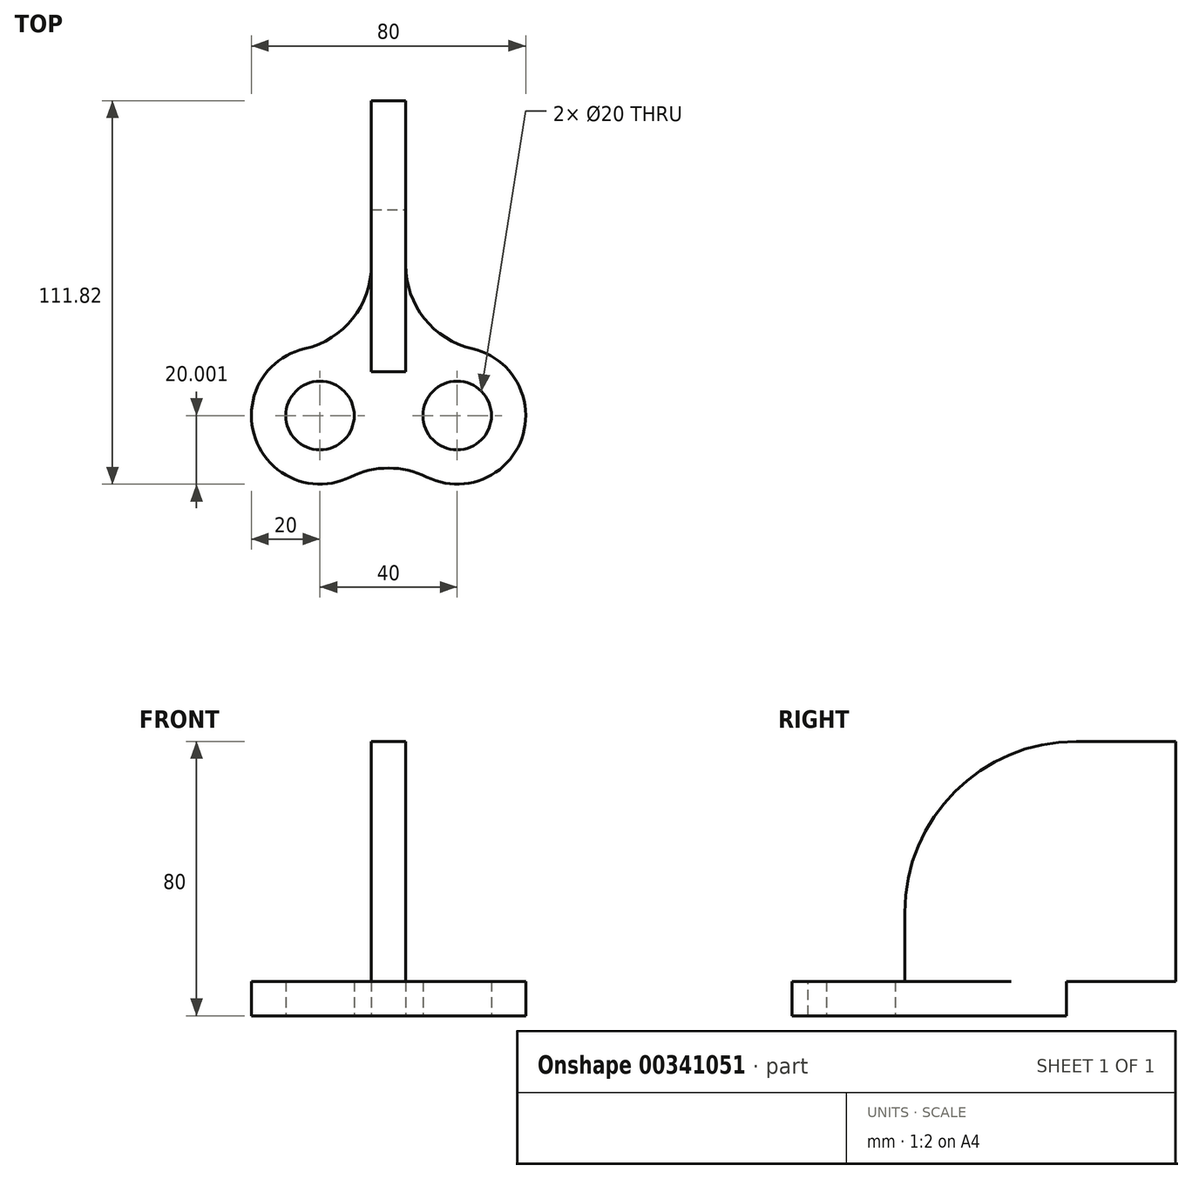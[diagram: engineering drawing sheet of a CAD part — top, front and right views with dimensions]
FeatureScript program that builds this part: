
annotation { "Feature Type Name" : "Feature", "Feature Type Description" : "" }
export const myFeature = defineFeature(function(context is Context, id is Id, definition is map)
    precondition{}
    {
        {
            var Q0;
            Q0=qCreatedBy(makeId("Top.planeOp"),FACE);
            var sketch = newSketch(context, id + "F0", { "sketchPlane" : qUnion([Q0])});
            skCircle(sketch, "E0", {"center": v(-20, 10.75) * mm, "radius": 20 * mm});
            skCircle(sketch, "E1", {"center": v(20, 10.75) * mm, "radius": 20 * mm});
            skCircle(sketch, "E2", {"center": v(-20, 10.75) * mm, "radius": 10 * mm});
            skCircle(sketch, "E3", {"center": v(20, 10.75) * mm, "radius": 10 * mm});
            skLineSegment(sketch, "E4.bottom", {"start": v(-5, 70.75) * mm, "end": v(5, 70.75) * mm});
            skLineSegment(sketch, "E4.top", {"start": v(-5, 10.75) * mm, "end": v(5, 10.75) * mm});
            skLineSegment(sketch, "E4.left", {"start": v(-5, 70.75) * mm, "end": v(-5, 10.75) * mm});
            skLineSegment(sketch, "E4.right", {"start": v(5, 70.75) * mm, "end": v(5, 10.75) * mm});
            skSolve(sketch);
        }
        {
            var Q0;
            Q0 = qSketchRegion(id + "F0", true);
            extrude(context, id + "F1", {"entities" : qUnion([Q0]), "depth" : 10 * mm});
        }
        {
            var Q0;
            {var subQ0=sQuery(id+"F0.wireOp",EDGE,"E1");var subQ1=sQuery(id+"F0.wireOp",EDGE,"E0");Q0=makeQuery(id+"F1.opExtrude","SWEPT_EDGE",EDGE,{"disambiguationData":[OSD([subQ1,subQ0]),TDD([makeQuery(id+"F0.imprint","INTERSECT",VERTEX,{"disambiguationData":[OD(0.0)],"derivedFrom":[subQ1,subQ0]})])]});}
            fillet(context, id + "F2", {"entities" : qUnion([Q0]), "radius" : 25 * mm, "tangentPropagation" : true, "allowEdgeOverflow" : false});
        }
        {
            var Q0;
            Q0=makeQuery(id+"F1.opExtrude","SWEPT_EDGE",EDGE,{"disambiguationData":[OSD([sQuery(id+"F0.wireOp",EDGE,"E1"),sQuery(id+"F0.wireOp",EDGE,"MdeKFbDD-k6u2-4Ekk-Ma7V-SLWvGI0NKfqd.right")])]});
            var Q1;
            Q1=makeQuery(id+"F1.opExtrude","SWEPT_EDGE",EDGE,{"disambiguationData":[OSD([sQuery(id+"F0.wireOp",EDGE,"E0"),sQuery(id+"F0.wireOp",EDGE,"MdeKFbDD-k6u2-4Ekk-Ma7V-SLWvGI0NKfqd.left")])]});
            fillet(context, id + "F3", {"entities" : qUnion([Q0, Q1]), "radius" : 25 * mm, "tangentPropagation" : true, "allowEdgeOverflow" : false});
        }
        {
            var Q0;
            Q0=makeQuery(id+"F1.opExtrude","CAP_FACE",FACE,{"disambiguationData":[OSD([sQuery(id+"F0.wireOp",EDGE,"E0"),sQuery(id+"F0.wireOp",EDGE,"E1"),sQuery(id+"F0.wireOp",EDGE,"E2"),sQuery(id+"F0.wireOp",EDGE,"E3"),sQuery(id+"F0.wireOp",EDGE,"E4.bottom"),sQuery(id+"F0.wireOp",EDGE,"E4.left"),sQuery(id+"F0.wireOp",EDGE,"E4.right")])],"isStart":false});
            var sketch = newSketch(context, id + "F4", { "sketchPlane" : qUnion([Q0])});
            skLineSegment(sketch, "E5.bottom", {"start": v(-5, 102.57) * mm, "end": v(5, 102.57) * mm});
            skLineSegment(sketch, "E5.top", {"start": v(-5, 23.57) * mm, "end": v(5, 23.57) * mm});
            skLineSegment(sketch, "E5.left", {"start": v(-5, 102.57) * mm, "end": v(-5, 23.57) * mm});
            skLineSegment(sketch, "E5.right", {"start": v(5, 102.57) * mm, "end": v(5, 23.57) * mm});
            skSolve(sketch);
        }
        {
            var Q0;
            Q0 = qSketchRegion(id + "F4", true);
            extrude(context, id + "F5", {"entities" : qUnion([Q0]), "operationType" : NewBodyOperationType.ADD, "depth" : 70 * mm});
        }
        {
            var Q0;
            Q0=makeQuery(id+"F5.opExtrude","CAP_EDGE",EDGE,{"disambiguationData":[OSD([sQuery(id+"F4.wireOp",EDGE,"E5.top")])],"isStart":false});
            fillet(context, id + "F6", {"entities" : qUnion([Q0]), "radius" : 50 * mm, "tangentPropagation" : true, "allowEdgeOverflow" : false});
        }
    });
